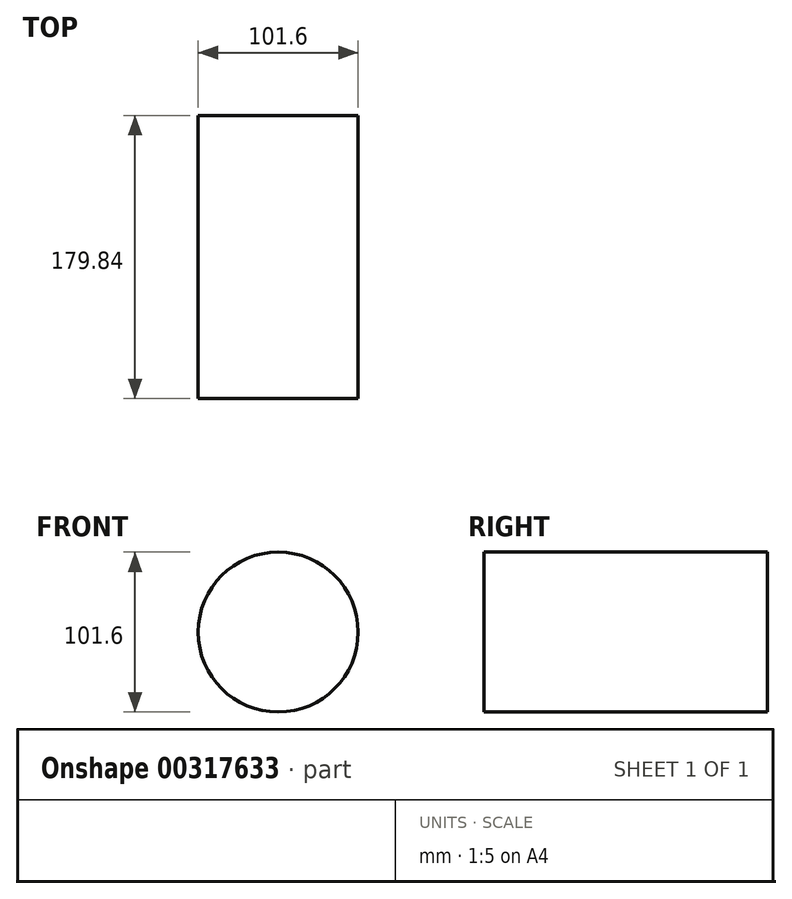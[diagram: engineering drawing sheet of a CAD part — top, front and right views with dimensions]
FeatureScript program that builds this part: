
annotation { "Feature Type Name" : "Feature", "Feature Type Description" : "" }
export const myFeature = defineFeature(function(context is Context, id is Id, definition is map)
    precondition{}
    {
        {
            var Q0;
            Q0=qCreatedBy(makeId("Front.planeOp"),FACE);
            var sketch = newSketch(context, id + "F0", { "sketchPlane" : qUnion([Q0])});
            skCircle(sketch, "E0", {"center": v(0, 0) * mm, "radius": 50.8 * mm});
            skSolve(sketch);
        }
        {
            var Q0;
            Q0 = qSketchRegion(id + "F0", true);
            extrude(context, id + "F1", {"entities" : qUnion([Q0]), "depth" : 139.45 * mm});
        }
        {
            var Q0;
            Q0=qCreatedBy(makeId("Front.planeOp"),FACE);
            var sketch = newSketch(context, id + "F2", { "sketchPlane" : qUnion([Q0])});
            skCircle(sketch, "E1", {"center": v(0, 0) * mm, "radius": 5.46 * mm});
            skLineSegment(sketch, "E2", {"start": v(5.46, 0) * mm, "end": v(50.8, 0) * mm});
            skLineSegment(sketch, "E3", {"start": v(0, 50.37) * mm, "end": v(0, 5.46) * mm});
            skLineSegment(sketch, "E4", {"start": v(0, -5.46) * mm, "end": v(0, -50.8) * mm});
            skLineSegment(sketch, "E5", {"start": v(-5.46, 0) * mm, "end": v(-50.8, 0) * mm});
            skSolve(sketch);
        }
        {
            var Q0;
            {var subQ0=sQuery(id+"F2.wireOp",EDGE,"E1");var subQ1=makeQuery(id+"F2.imprint","IMPRINT",VERTEX,{"disambiguationData":[OD(0.0)],"derivedFrom":subQ0});Q0=makeQuery(id+"F2.imprint","IMPRINT",FACE,{"disambiguationData":[TD([[makeQuery(id+"F2.imprint","IMPRINT",EDGE,{"disambiguationData":[TD([[subQ1,-1.0]])],"derivedFrom":subQ0}),1.0]])]});}
            var Q1;
            Q1=makeQuery(id+"F1.opExtrude","CAP_FACE",FACE,{"disambiguationData":[OSD([sQuery(id+"F0.wireOp",EDGE,"E0")])],"isStart":true});
            var Q2;
            Q2=makeQuery(id+"F1.opExtrude","CAP_FACE",FACE,{"disambiguationData":[OSD([sQuery(id+"F0.wireOp",EDGE,"E0")])],"isStart":false});
            extrude(context, id + "F3", {"entities" : qUnion([Q0, Q1, Q2]), "operationType" : NewBodyOperationType.ADD, "oppositeDirection" : true, "depth" : 40.4 * mm});
        }
    });
